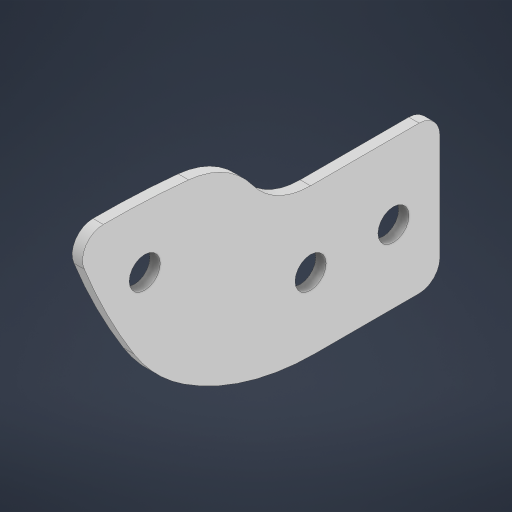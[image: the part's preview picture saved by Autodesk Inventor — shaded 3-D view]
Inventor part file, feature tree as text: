
AUTODESK INVENTOR PART (.ipt)
format: ipt  version: 2024 (Build 280153000, 153)  size: 223,744 bytes
history: native  units: in
note: dims shown in document units (in); Inventor stores cm internally (conversion verified against a paired STEP export)
features: sketch x1, extrude x1, hole x1
ambient origin geometry x8: Origin, YZ Plane, XZ Plane, XY Plane, X Axis, Y Axis, Z Axis, Center Point
bodies: Solid1 (feature_tree)
feature tree (3):
  sketch  "Sketch2"  dims[d0=1.0in d1=0.5in d2=0.25in d3=0.25in d4=1.25in d5=1.0in d7=1.0in d8=0.5in d12=1.0in d17=0.75in d18=1.0in d19=0.0625in d20=0.0in d21=0.125in d22=0.1875in d23=0.75in d24=0.375in d25=0.25in d26=0.5635in d27=1.0in d28=0.8108in d29=0.5in]
  extrude  "Extrusion1"  Depth=1.0in
  hole  "Hole1"  [1 undecoded]
note: 1 required parameter value undecoded (feature->parameter linkage not recoverable at this tier; creation-order binding heuristic only, values carry confidence <= 0.55)
